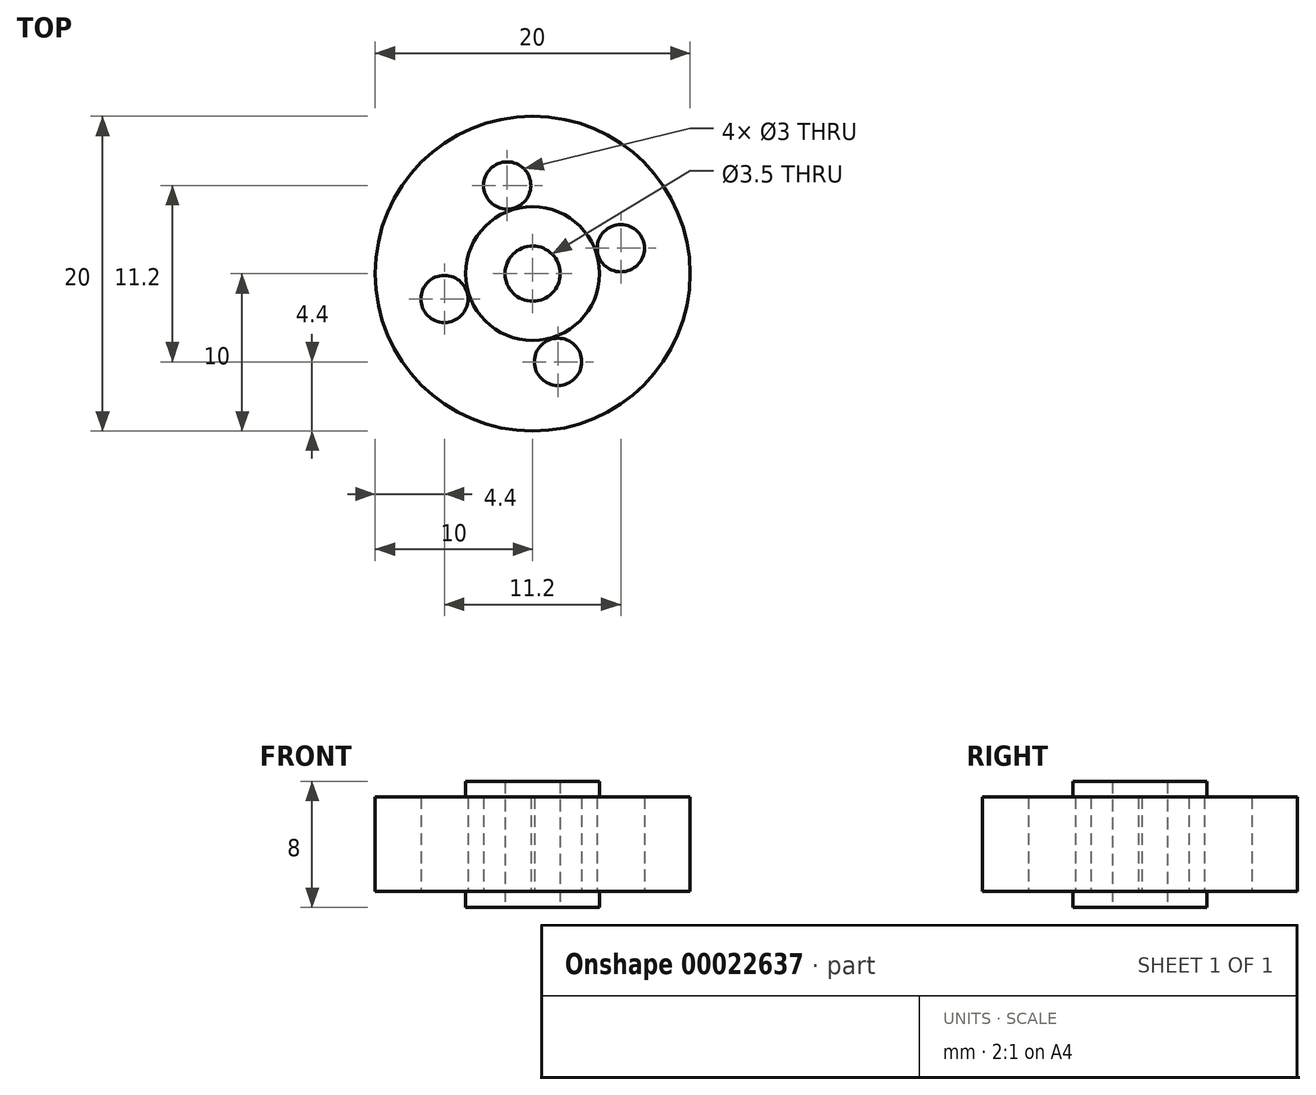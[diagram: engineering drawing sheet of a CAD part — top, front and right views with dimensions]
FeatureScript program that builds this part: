
annotation { "Feature Type Name" : "Feature", "Feature Type Description" : "" }
export const myFeature = defineFeature(function(context is Context, id is Id, definition is map)
    precondition{}
    {
        {
            var Q0;
            Q0=qCreatedBy(makeId("Top.planeOp"),FACE);
            var sketch = newSketch(context, id + "F0", { "sketchPlane" : qUnion([Q0])});
            skCircle(sketch, "E0", {"center": v(0, 0) * mm, "radius": 10 * mm});
            skCircle(sketch, "E1", {"center": v(0, 0) * mm, "radius": 1.75 * mm});
            skCircle(sketch, "E2", {"center": v(0, 0) * mm, "radius": 4.25 * mm});
            skCircle(sketch, "E3", {"center": v(-5.6, -1.61) * mm, "radius": 1.5 * mm});
            skCircle(sketch, "E4.1.0", {"center": v(1.61, -5.6) * mm, "radius": 1.5 * mm});
            skCircle(sketch, "E4.2.0", {"center": v(5.6, 1.61) * mm, "radius": 1.5 * mm});
            skCircle(sketch, "E5.1.3.0", {"center": v(-1.61, 5.6) * mm, "radius": 1.5 * mm});
            skSolve(sketch);
        }
        {
            var Q0;
            Q0=makeQuery(id+"F0.imprint","IMPRINT",FACE,{"disambiguationData":[TD([[makeQuery(id+"F0.imprint","IMPRINT",EDGE,{"derivedFrom":sQuery(id+"F0.wireOp",EDGE,"E0")}),1.0]])]});
            extrude(context, id + "F1", {"entities" : qUnion([Q0]), "endBound" : BoundingType.SYMMETRIC, "depth" : 6 * mm});
        }
        {
            var Q0;
            Q0=makeQuery(id+"F0.imprint","IMPRINT",FACE,{"disambiguationData":[TD([[makeQuery(id+"F0.imprint","IMPRINT",EDGE,{"derivedFrom":sQuery(id+"F0.wireOp",EDGE,"E1")}),-1.0]])]});
            extrude(context, id + "F2", {"entities" : qUnion([Q0]), "operationType" : NewBodyOperationType.ADD, "endBound" : BoundingType.SYMMETRIC, "depth" : 8 * mm});
        }
    });
